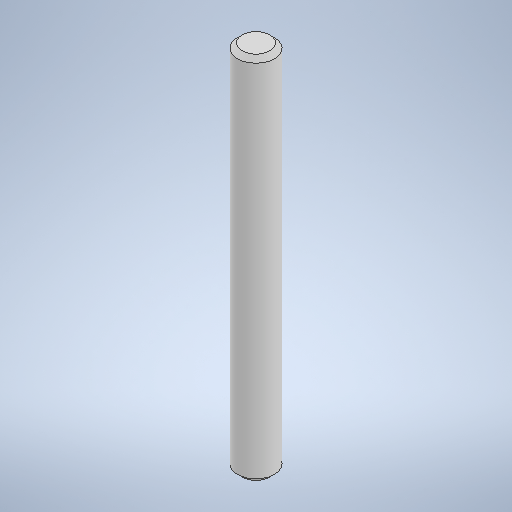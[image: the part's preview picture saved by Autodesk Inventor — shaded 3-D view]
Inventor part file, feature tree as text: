
AUTODESK INVENTOR PART (.ipt)
format: ipt  version: 2025.1 (Build 291241000, 241)  size: 245,760 bytes
history: native  units: mm
features: extrude x1, chamfer x1, sketch x1
ambient origin geometry x8: Origin, YZ Plane, XZ Plane, XY Plane, X Axis, Y Axis, Z Axis, Center Point
bodies: Solid1 (feature_tree)
feature tree (3):
  extrude  "Extrusion1"  Depth=20.0mm TaperAngle=0.0deg
  chamfer  "Chamfer1"  Distance=0.25mm Angle=45.0deg
  sketch  "Sketch1"  dims[d0=2.0mm d1=20.0mm d2=0.0mm d3=0.25mm d4=2.0mm d5=45.0deg]
